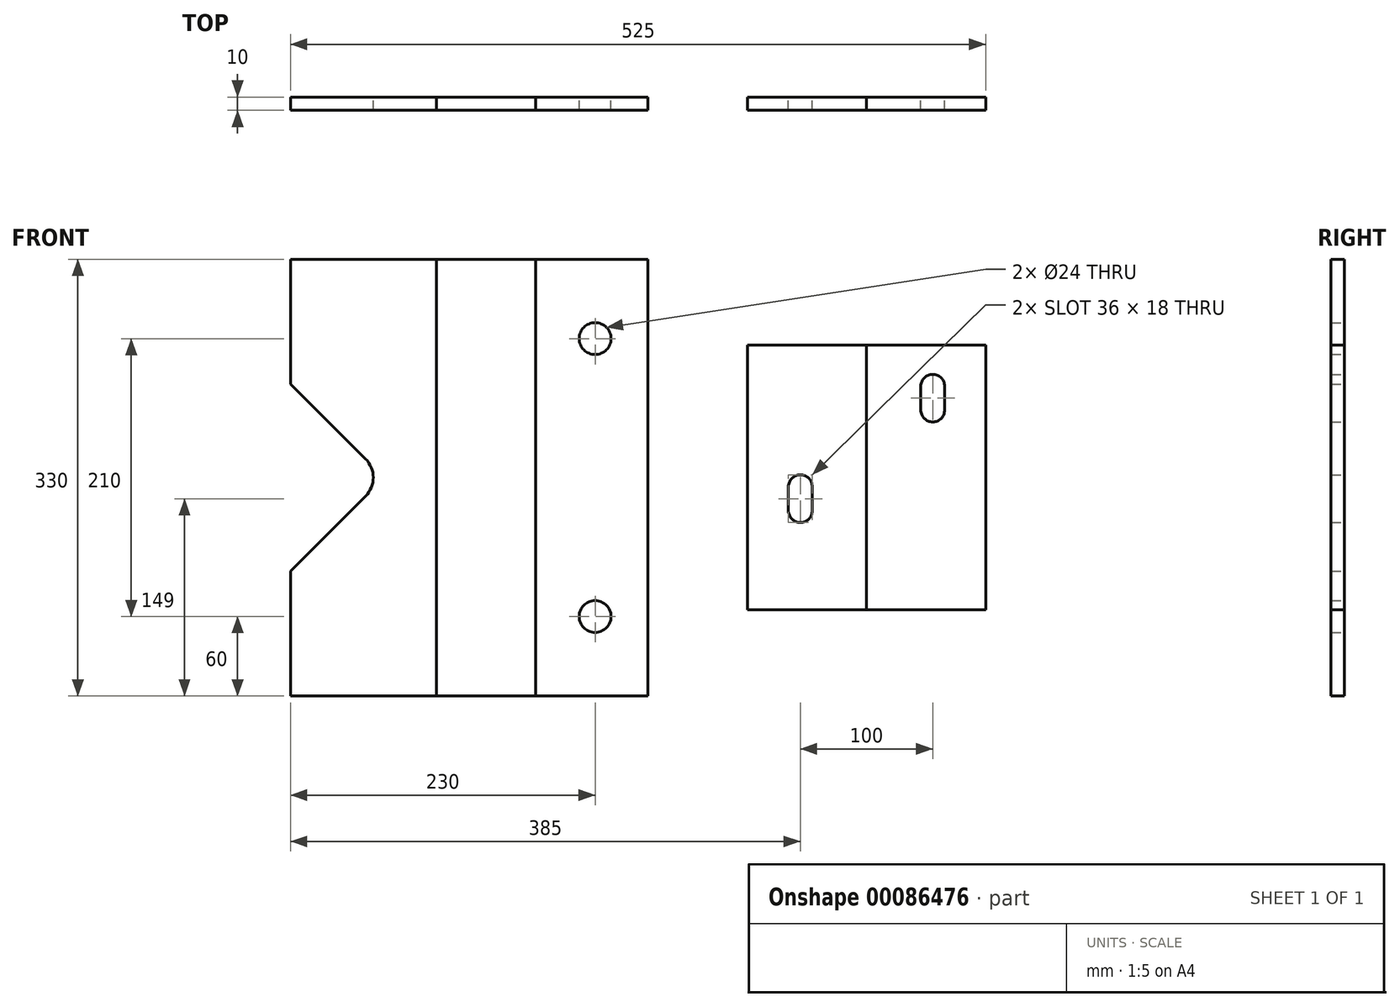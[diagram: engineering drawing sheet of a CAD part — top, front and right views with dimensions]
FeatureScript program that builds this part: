
annotation { "Feature Type Name" : "Feature", "Feature Type Description" : "" }
export const myFeature = defineFeature(function(context is Context, id is Id, definition is map)
    precondition{}
    {
        {
            var Q0;
            Q0=qCreatedBy(makeId("Front.planeOp"),FACE);
            var sketch = newSketch(context, id + "F0", { "sketchPlane" : qUnion([Q0])});
            skLineSegment(sketch, "E0.bottom", {"start": v(135, 165) * mm, "end": v(-135, 165) * mm});
            skLineSegment(sketch, "E0.top", {"start": v(135, -165) * mm, "end": v(-135, -165) * mm});
            skLineSegment(sketch, "E0.left", {"start": v(135, 165) * mm, "end": v(135, -165) * mm});
            skLineSegment(sketch, "E0.right", {"start": v(-135, 165) * mm, "end": v(-135, -165) * mm});
            skPoint(sketch, "E0.middle", {"position": v(0, 0) * mm});
            skLineSegment(sketch, "E1", {"start": v(-25, 165) * mm, "end": v(-25, -165) * mm});
            skLineSegment(sketch, "E2", {"start": v(50, 165) * mm, "end": v(50, -165) * mm});
            skLineSegment(sketch, "E3", {"start": v(95, 165) * mm, "end": v(95, -165) * mm, "construction": true});
            skPoint(sketch, "E4", {"position": v(95, 105) * mm});
            skCircle(sketch, "E5", {"center": v(95, 105) * mm, "radius": 12 * mm});
            skCircle(sketch, "E6.MirrorC", {"center": v(95, -105) * mm, "radius": 12 * mm});
            skLineSegment(sketch, "E7", {"start": v(0, 0) * mm, "end": v(300, 0) * mm, "construction": true});
            skLineSegment(sketch, "E8.bottom", {"start": v(390, 100) * mm, "end": v(210, 100) * mm});
            skLineSegment(sketch, "E8.top", {"start": v(390, -100) * mm, "end": v(210, -100) * mm});
            skLineSegment(sketch, "E8.left", {"start": v(390, 100) * mm, "end": v(390, -100) * mm});
            skLineSegment(sketch, "E8.right", {"start": v(210, 100) * mm, "end": v(210, -100) * mm});
            skPoint(sketch, "E8.middle", {"position": v(300, 0) * mm});
            skLineSegment(sketch, "E9", {"start": v(300, 100) * mm, "end": v(300, -100) * mm});
            skLineSegment(sketch, "E10", {"start": v(250, 100) * mm, "end": v(250, -100) * mm, "construction": true});
            skLineSegment(sketch, "E11.MirrorCS", {"start": v(350, 100) * mm, "end": v(350, -100) * mm, "construction": true});
            skLineSegment(sketch, "E12", {"start": v(210, -16) * mm, "end": v(300, -16) * mm, "construction": true});
            skLineSegment(sketch, "E13", {"start": v(300, 60) * mm, "end": v(390, 60) * mm, "construction": true});
            skLineSegment(sketch, "E14.bottom", {"start": v(259, 2) * mm, "end": v(241, 2) * mm});
            skLineSegment(sketch, "E14.top", {"start": v(259, -34) * mm, "end": v(241, -34) * mm});
            skLineSegment(sketch, "E14.left", {"start": v(259, 2) * mm, "end": v(259, -34) * mm});
            skLineSegment(sketch, "E14.right", {"start": v(241, 2) * mm, "end": v(241, -34) * mm});
            skPoint(sketch, "E14.middle", {"position": v(250, -16) * mm});
            skLineSegment(sketch, "E15.bottom", {"start": v(359, 78) * mm, "end": v(341, 78) * mm});
            skLineSegment(sketch, "E15.top", {"start": v(359, 42) * mm, "end": v(341, 42) * mm});
            skLineSegment(sketch, "E15.left", {"start": v(359, 78) * mm, "end": v(359, 42) * mm});
            skLineSegment(sketch, "E15.right", {"start": v(341, 78) * mm, "end": v(341, 42) * mm});
            skPoint(sketch, "E15.middle", {"position": v(350, 60) * mm});
            skPoint(sketch, "E16", {"position": v(250, -7) * mm});
            skArc(sketch, "E17", {"start": v(259, -7) * mm, "mid": v(250, 2) * mm, "end": v(241, -7) * mm});
            skPoint(sketch, "E17.first.point", {"position": v(250, 2) * mm});
            skPoint(sketch, "E17.third.point", {"position": v(241, -7) * mm});
            skArc(sketch, "E18.MirrorCS", {"start": v(259, -25) * mm, "mid": v(250, -34) * mm, "end": v(241, -25) * mm});
            skPoint(sketch, "E19", {"position": v(350, 69) * mm});
            skArc(sketch, "E20", {"start": v(359, 69) * mm, "mid": v(350, 78) * mm, "end": v(341, 69) * mm});
            skPoint(sketch, "E20.first.point", {"position": v(350, 78) * mm});
            skPoint(sketch, "E20.third.point", {"position": v(341, 69) * mm});
            skArc(sketch, "E21.MirrorCS", {"start": v(359, 51) * mm, "mid": v(350, 42) * mm, "end": v(341, 51) * mm});
            skLineSegment(sketch, "E22", {"start": v(0, 0) * mm, "end": v(-135, 0) * mm, "construction": true});
            skLineSegment(sketch, "E23", {"start": v(-78.43, 14.14) * mm, "end": v(-135, 70.71) * mm});
            skLineSegment(sketch, "E24", {"start": v(-78.43, -14.14) * mm, "end": v(-135, -70.71) * mm});
            skPoint(sketch, "E25.visualSharp", {"position": v(-64.29, 0) * mm});
            skArc(sketch, "E25.filletArc", {"start": v(-78.43, -14.14) * mm, "mid": v(-72.57, 0) * mm, "end": v(-78.43, 14.14) * mm});
            skSolve(sketch);
        }
        {
            var Q0;
            {var subQ4=sQuery(id+"F0.wireOp",EDGE,"E1");Q0=makeQuery(id+"F0.imprint","IMPRINT",FACE,{"disambiguationData":[TD([[makeQuery(id+"F0.imprint","IMPRINT",EDGE,{"derivedFrom":subQ4}),-1.0]])]});}
            var Q1;
            {var subQ14=sQuery(id+"F0.wireOp",EDGE,"E8.right");Q1=makeQuery(id+"F0.imprint","IMPRINT",FACE,{"disambiguationData":[TD([[makeQuery(id+"F0.imprint","IMPRINT",EDGE,{"derivedFrom":subQ14}),1.0]])]});}
            var Q2;
            {var subQ0=sQuery(id+"F0.wireOp",EDGE,"E14.left");var subQ1=sQuery(id+"F0.wireOp",EDGE,"E14.top");var subQ2=makeQuery(id+"F0.imprint","INTERSECT",VERTEX,{"derivedFrom":[subQ1,subQ0]});Q2=makeQuery(id+"F0.imprint","IMPRINT",FACE,{"disambiguationData":[TD([[makeQuery(id+"F0.imprint","IMPRINT",EDGE,{"disambiguationData":[TD([[subQ2,-1.0]])],"derivedFrom":subQ1}),-1.0]])]});}
            var Q3;
            {var subQ0=sQuery(id+"F0.wireOp",EDGE,"E14.left");var subQ1=sQuery(id+"F0.wireOp",EDGE,"E14.bottom");var subQ2=makeQuery(id+"F0.imprint","INTERSECT",VERTEX,{"derivedFrom":[subQ1,subQ0]});Q3=makeQuery(id+"F0.imprint","IMPRINT",FACE,{"disambiguationData":[TD([[makeQuery(id+"F0.imprint","IMPRINT",EDGE,{"disambiguationData":[TD([[subQ2,-1.0]])],"derivedFrom":subQ1}),1.0]])]});}
            var Q4;
            {var subQ0=sQuery(id+"F0.wireOp",EDGE,"E14.right");var subQ1=sQuery(id+"F0.wireOp",EDGE,"E14.bottom");var subQ2=makeQuery(id+"F0.imprint","INTERSECT",VERTEX,{"derivedFrom":[subQ1,subQ0]});Q4=makeQuery(id+"F0.imprint","IMPRINT",FACE,{"disambiguationData":[TD([[makeQuery(id+"F0.imprint","IMPRINT",EDGE,{"disambiguationData":[TD([[subQ2,1.0]])],"derivedFrom":subQ1}),1.0]])]});}
            var Q5;
            {var subQ0=sQuery(id+"F0.wireOp",EDGE,"E14.right");var subQ1=sQuery(id+"F0.wireOp",EDGE,"E14.top");var subQ2=makeQuery(id+"F0.imprint","INTERSECT",VERTEX,{"derivedFrom":[subQ1,subQ0]});Q5=makeQuery(id+"F0.imprint","IMPRINT",FACE,{"disambiguationData":[TD([[makeQuery(id+"F0.imprint","IMPRINT",EDGE,{"disambiguationData":[TD([[subQ2,1.0]])],"derivedFrom":subQ1}),-1.0]])]});}
            extrude(context, id + "F1", {"entities" : qUnion([Q0, Q1, Q2, Q3, Q4, Q5]), "depth" : 10 * mm});
        }
        {
            var Q0;
            {var subQ1=sQuery(id+"F0.wireOp",EDGE,"E0.left");Q0=makeQuery(id+"F0.imprint","IMPRINT",FACE,{"disambiguationData":[TD([[makeQuery(id+"F0.imprint","IMPRINT",EDGE,{"derivedFrom":subQ1}),-1.0]])]});}
            var Q1;
            {var subQ14=sQuery(id+"F0.wireOp",EDGE,"E8.left");Q1=makeQuery(id+"F0.imprint","IMPRINT",FACE,{"disambiguationData":[TD([[makeQuery(id+"F0.imprint","IMPRINT",EDGE,{"derivedFrom":subQ14}),-1.0]])]});}
            var Q2;
            {var subQ0=sQuery(id+"F0.wireOp",EDGE,"E15.right");var subQ1=sQuery(id+"F0.wireOp",EDGE,"E15.bottom");var subQ2=makeQuery(id+"F0.imprint","INTERSECT",VERTEX,{"derivedFrom":[subQ1,subQ0]});Q2=makeQuery(id+"F0.imprint","IMPRINT",FACE,{"disambiguationData":[TD([[makeQuery(id+"F0.imprint","IMPRINT",EDGE,{"disambiguationData":[TD([[subQ2,1.0]])],"derivedFrom":subQ1}),1.0]])]});}
            var Q3;
            {var subQ0=sQuery(id+"F0.wireOp",EDGE,"E15.left");var subQ1=sQuery(id+"F0.wireOp",EDGE,"E15.bottom");var subQ2=makeQuery(id+"F0.imprint","INTERSECT",VERTEX,{"derivedFrom":[subQ1,subQ0]});Q3=makeQuery(id+"F0.imprint","IMPRINT",FACE,{"disambiguationData":[TD([[makeQuery(id+"F0.imprint","IMPRINT",EDGE,{"disambiguationData":[TD([[subQ2,-1.0]])],"derivedFrom":subQ1}),1.0]])]});}
            var Q4;
            {var subQ0=sQuery(id+"F0.wireOp",EDGE,"E15.left");var subQ1=sQuery(id+"F0.wireOp",EDGE,"E15.top");var subQ2=makeQuery(id+"F0.imprint","INTERSECT",VERTEX,{"derivedFrom":[subQ1,subQ0]});Q4=makeQuery(id+"F0.imprint","IMPRINT",FACE,{"disambiguationData":[TD([[makeQuery(id+"F0.imprint","IMPRINT",EDGE,{"disambiguationData":[TD([[subQ2,-1.0]])],"derivedFrom":subQ1}),-1.0]])]});}
            var Q5;
            {var subQ0=sQuery(id+"F0.wireOp",EDGE,"E15.right");var subQ1=sQuery(id+"F0.wireOp",EDGE,"E15.top");var subQ2=makeQuery(id+"F0.imprint","INTERSECT",VERTEX,{"derivedFrom":[subQ1,subQ0]});Q5=makeQuery(id+"F0.imprint","IMPRINT",FACE,{"disambiguationData":[TD([[makeQuery(id+"F0.imprint","IMPRINT",EDGE,{"disambiguationData":[TD([[subQ2,1.0]])],"derivedFrom":subQ1}),-1.0]])]});}
            extrude(context, id + "F2", {"entities" : qUnion([Q0, Q1, Q2, Q3, Q4, Q5]), "depth" : 10 * mm});
        }
        {
            var Q0;
            {var subQ0=sQuery(id+"F0.wireOp",EDGE,"E1");Q0=makeQuery(id+"F0.imprint","IMPRINT",FACE,{"disambiguationData":[TD([[makeQuery(id+"F0.imprint","IMPRINT",EDGE,{"derivedFrom":subQ0}),1.0]])]});}
            extrude(context, id + "F3", {"entities" : qUnion([Q0]), "depth" : 10 * mm});
        }
    });
